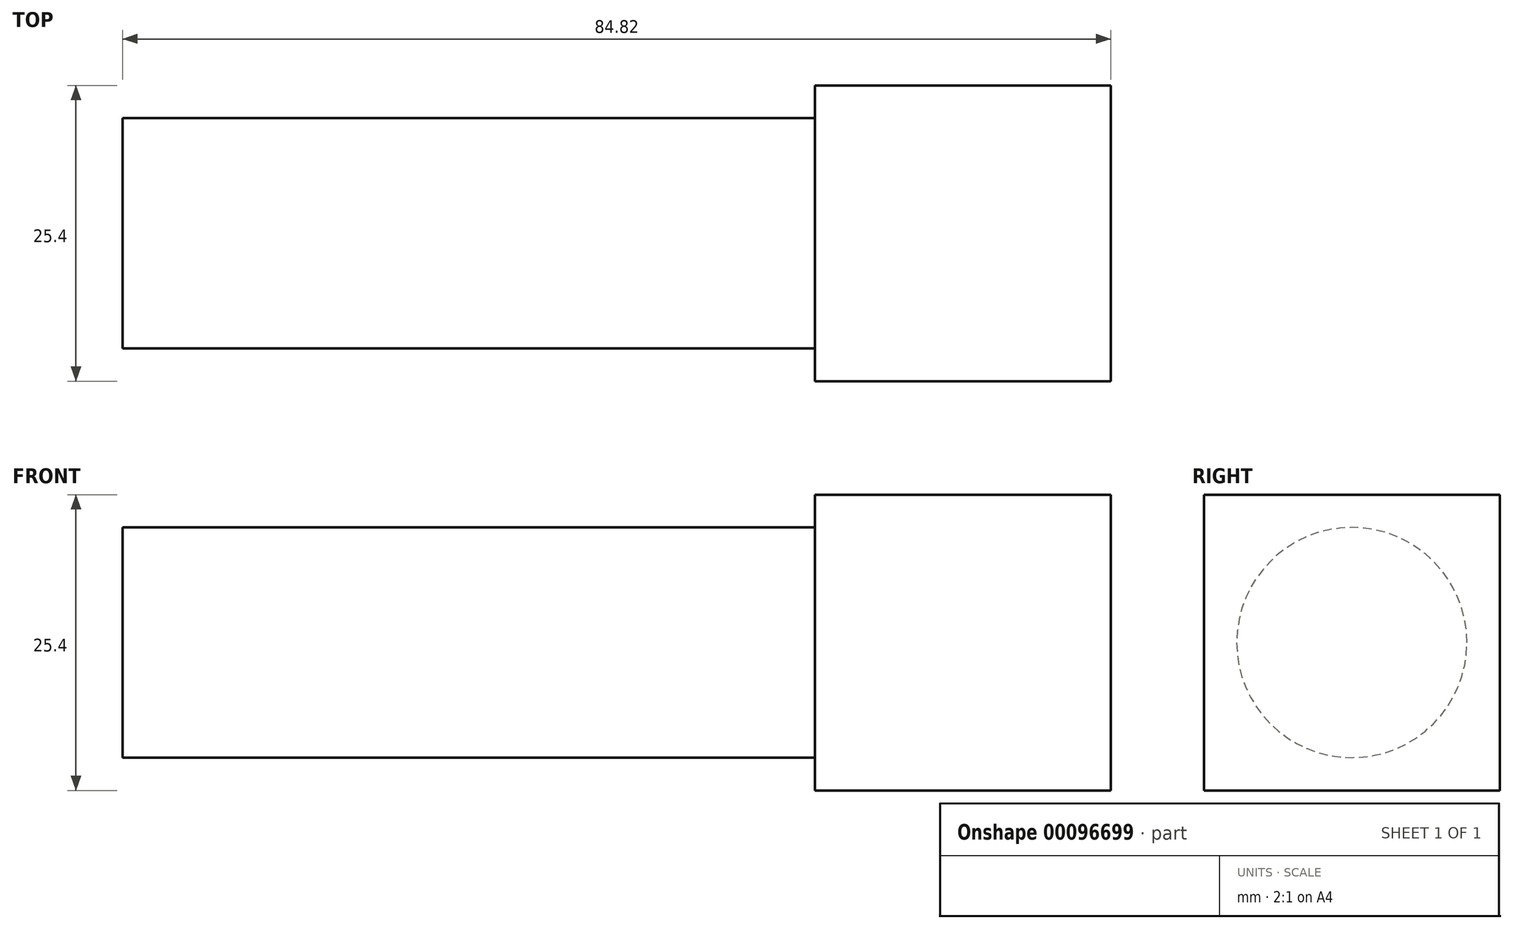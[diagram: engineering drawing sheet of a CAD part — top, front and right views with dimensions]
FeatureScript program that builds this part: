
annotation { "Feature Type Name" : "Feature", "Feature Type Description" : "" }
export const myFeature = defineFeature(function(context is Context, id is Id, definition is map)
    precondition{}
    {
        {
            var Q0;
            Q0=qCreatedBy(makeId("Top.planeOp"),FACE);
            var sketch = newSketch(context, id + "F0", { "sketchPlane" : qUnion([Q0])});
            skLineSegment(sketch, "E0.bottom", {"start": v(-12.27, 8) * mm, "end": v(13.13, 8) * mm});
            skLineSegment(sketch, "E0.top", {"start": v(-12.27, -17.4) * mm, "end": v(13.13, -17.4) * mm});
            skLineSegment(sketch, "E0.left", {"start": v(-12.27, 8) * mm, "end": v(-12.27, -17.4) * mm});
            skLineSegment(sketch, "E0.right", {"start": v(13.13, 8) * mm, "end": v(13.13, -17.4) * mm});
            skSolve(sketch);
        }
        {
            var Q0;
            Q0=makeQuery(id+"F0.imprint","IMPRINT",FACE,{"disambiguationData":[TD([[makeQuery(id+"F0.imprint","IMPRINT",EDGE,{"derivedFrom":sQuery(id+"F0.wireOp",EDGE,"E0.bottom")}),-1.0]])]});
            extrude(context, id + "F1", {"entities" : qUnion([Q0]), "depth" : 25.4 * mm});
        }
        {
            var Q0;
            Q0=makeQuery(id+"F1.opExtrude","SWEPT_FACE",FACE,{"disambiguationData":[OSD([sQuery(id+"F0.wireOp",EDGE,"E0.left")])]});
            var sketch = newSketch(context, id + "F2", { "sketchPlane" : qUnion([Q0])});
            skCircle(sketch, "E1", {"center": v(4.7, 12.7) * mm, "radius": 9.88 * mm});
            skPoint(sketch, "E1.centerSnap0", {"position": v(4.7, 25.4) * mm});
            skPoint(sketch, "E1.centerSnap1", {"position": v(-8, 12.7) * mm});
            skSolve(sketch);
        }
        {
            var Q0;
            Q0=makeQuery(id+"F2.imprint","IMPRINT",FACE,{"disambiguationData":[TD([[makeQuery(id+"F2.imprint","IMPRINT",EDGE,{"derivedFrom":sQuery(id+"F2.wireOp",EDGE,"E1")}),1.0]])]});
            extrude(context, id + "F3", {"entities" : qUnion([Q0]), "operationType" : NewBodyOperationType.ADD, "depth" : 59.42 * mm});
        }
    });
